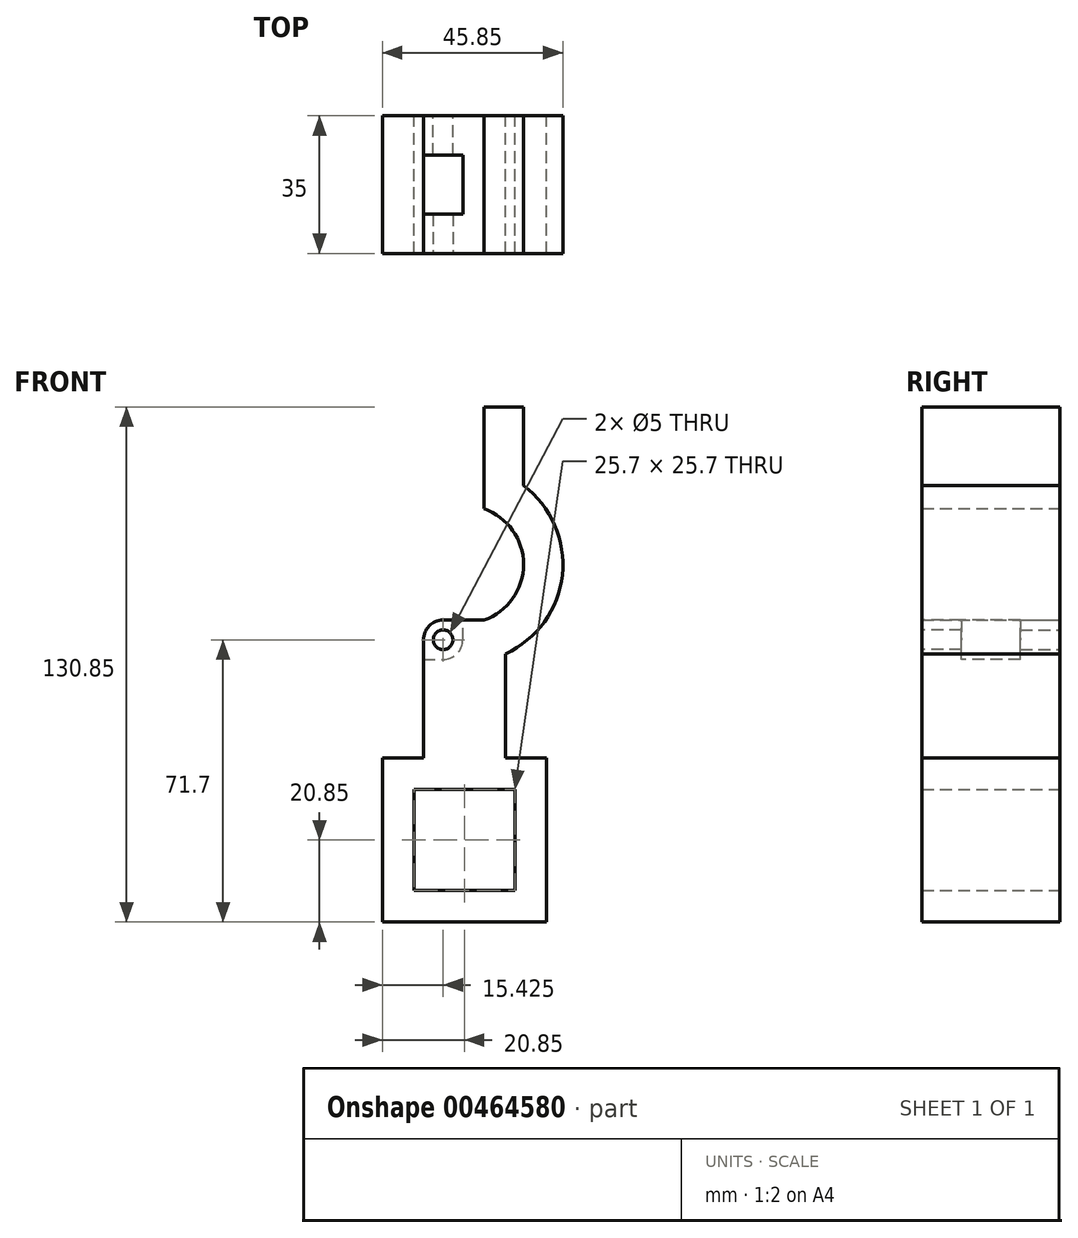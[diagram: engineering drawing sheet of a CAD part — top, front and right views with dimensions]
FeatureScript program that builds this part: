
annotation { "Feature Type Name" : "Feature", "Feature Type Description" : "" }
export const myFeature = defineFeature(function(context is Context, id is Id, definition is map)
    precondition{}
    {
        {
            var Q0;
            Q0=qCreatedBy(makeId("Front.planeOp"),FACE);
            var sketch = newSketch(context, id + "F0", { "sketchPlane" : qUnion([Q0])});
            skLineSegment(sketch, "E0", {"start": v(0, 0) * mm, "end": v(0, 12.85) * mm, "construction": true});
            skLineSegment(sketch, "E1", {"start": v(0, 12.85) * mm, "end": v(12.85, 12.85) * mm});
            skLineSegment(sketch, "E2", {"start": v(12.85, 12.85) * mm, "end": v(12.85, 0) * mm});
            skLineSegment(sketch, "E3", {"start": v(12.85, 0) * mm, "end": v(0, 0) * mm, "construction": true});
            skLineSegment(sketch, "E4", {"start": v(12.85, 0) * mm, "end": v(12.85, -12.85) * mm});
            skLineSegment(sketch, "E5", {"start": v(12.85, -12.85) * mm, "end": v(0, -12.85) * mm});
            skLineSegment(sketch, "E6", {"start": v(0, -12.85) * mm, "end": v(0, 0) * mm, "construction": true});
            skLineSegment(sketch, "E7", {"start": v(0, 0) * mm, "end": v(-12.85, 0) * mm, "construction": true});
            skLineSegment(sketch, "E8", {"start": v(-12.85, 0) * mm, "end": v(-12.85, 12.85) * mm});
            skLineSegment(sketch, "E9", {"start": v(-12.85, 12.85) * mm, "end": v(0, 12.85) * mm});
            skLineSegment(sketch, "E10", {"start": v(-12.85, 0) * mm, "end": v(-12.85, -12.85) * mm});
            skLineSegment(sketch, "E11", {"start": v(-12.85, -12.85) * mm, "end": v(0, -12.85) * mm});
            skLineSegment(sketch, "E12", {"start": v(-12.85, 0) * mm, "end": v(-20.85, 0) * mm, "construction": true});
            skLineSegment(sketch, "E13", {"start": v(-20.85, 0) * mm, "end": v(-20.85, -20.85) * mm});
            skLineSegment(sketch, "E14", {"start": v(20.85, -20.85) * mm, "end": v(20.85, 0) * mm});
            skLineSegment(sketch, "E15", {"start": v(20.85, 0) * mm, "end": v(12.85, 0) * mm, "construction": true});
            skLineSegment(sketch, "E16", {"start": v(20.85, 0) * mm, "end": v(20.85, 20.85) * mm});
            skLineSegment(sketch, "E17", {"start": v(20.85, 20.85) * mm, "end": v(10.43, 20.85) * mm});
            skLineSegment(sketch, "E18", {"start": v(-20.85, 20.85) * mm, "end": v(-20.85, 0) * mm});
            skLineSegment(sketch, "E19", {"start": v(0, 20.85) * mm, "end": v(0, 12.85) * mm, "construction": true});
            skLineSegment(sketch, "E20", {"start": v(-20.85, -20.85) * mm, "end": v(0, -20.85) * mm});
            skLineSegment(sketch, "E21", {"start": v(0, -20.85) * mm, "end": v(20.85, -20.85) * mm});
            skLineSegment(sketch, "E22", {"start": v(0, -12.85) * mm, "end": v(0, -20.85) * mm, "construction": true});
            skLineSegment(sketch, "E23", {"start": v(10.43, 20.85) * mm, "end": v(10.43, 47.28) * mm});
            skLineSegment(sketch, "E24", {"start": v(-10.43, 20.85) * mm, "end": v(-10.43, 55.85) * mm});
            skLineSegment(sketch, "E25", {"start": v(-10.43, 55.85) * mm, "end": v(4.98, 55.85) * mm});
            skArc(sketch, "E26", {"start": v(10.43, 47.28) * mm, "mid": v(24.86, 67.34) * mm, "end": v(15, 90) * mm});
            skArc(sketch, "E27", {"start": v(4.98, 55.85) * mm, "mid": v(15, 69.99) * mm, "end": v(5, 84.14) * mm});
            skLineSegment(sketch, "E28", {"start": v(0, 70) * mm, "end": v(0, 110) * mm, "construction": true});
            skLineSegment(sketch, "E29", {"start": v(0, 110) * mm, "end": v(5, 110) * mm, "construction": true});
            skLineSegment(sketch, "E30", {"start": v(5, 110) * mm, "end": v(5, 84.14) * mm});
            skLineSegment(sketch, "E31", {"start": v(15, 90) * mm, "end": v(15, 110) * mm});
            skLineSegment(sketch, "E32", {"start": v(15, 110) * mm, "end": v(5, 110) * mm});
            skLineSegment(sketch, "E33", {"start": v(0, 110) * mm, "end": v(-5, 110) * mm, "construction": true});
            skLineSegment(sketch, "E34", {"start": v(-5.43, 55.85) * mm, "end": v(-5.43, 50.85) * mm, "construction": true});
            skLineSegment(sketch, "E35", {"start": v(-5.42, 50.85) * mm, "end": v(-10.43, 50.85) * mm, "construction": true});
            skCircle(sketch, "E36", {"center": v(-5.43, 50.85) * mm, "radius": 2.5 * mm});
            skPoint(sketch, "E37.orphan", {"position": v(10.43, 55.85) * mm});
            skLineSegment(sketch, "E38", {"start": v(-20.85, 20.85) * mm, "end": v(-10.43, 20.85) * mm});
            skSolve(sketch);
        }
        {
            var Q0;
            Q0=qSketchRegion(id+"F0",true);
            extrude(context, id + "F1", {"entities" : qUnion([Q0]), "depth" : 15 * mm});
        }
        {
            var Q0;
            Q0=makeQuery(id+"F1.opExtrude","SWEPT_EDGE",EDGE,{"disambiguationData":[OSD([sQuery(id+"F0.wireOp",EDGE,"E24"),sQuery(id+"F0.wireOp",EDGE,"E25")])]});
            fillet(context, id + "F2", {"entities" : qUnion([Q0]), "radius" : 5 * mm, "tangentPropagation" : true, "allowEdgeOverflow" : false});
        }
        {
            var Q0;
            Q0=makeQuery(id+"F1.opExtrude","CAP_FACE",FACE,{"disambiguationData":[OSD([sQuery(id+"F0.wireOp",EDGE,"E1"),sQuery(id+"F0.wireOp",EDGE,"E2"),sQuery(id+"F0.wireOp",EDGE,"E4"),sQuery(id+"F0.wireOp",EDGE,"E5"),sQuery(id+"F0.wireOp",EDGE,"E8"),sQuery(id+"F0.wireOp",EDGE,"E9"),sQuery(id+"F0.wireOp",EDGE,"E10"),sQuery(id+"F0.wireOp",EDGE,"E11"),sQuery(id+"F0.wireOp",EDGE,"E13"),sQuery(id+"F0.wireOp",EDGE,"E14"),sQuery(id+"F0.wireOp",EDGE,"E16"),sQuery(id+"F0.wireOp",EDGE,"E17"),sQuery(id+"F0.wireOp",EDGE,"E18"),sQuery(id+"F0.wireOp",EDGE,"E20"),sQuery(id+"F0.wireOp",EDGE,"E21"),sQuery(id+"F0.wireOp",EDGE,"E23"),sQuery(id+"F0.wireOp",EDGE,"E24"),sQuery(id+"F0.wireOp",EDGE,"E25"),sQuery(id+"F0.wireOp",EDGE,"E26"),sQuery(id+"F0.wireOp",EDGE,"E27"),sQuery(id+"F0.wireOp",EDGE,"E30"),sQuery(id+"F0.wireOp",EDGE,"E31"),sQuery(id+"F0.wireOp",EDGE,"E32"),sQuery(id+"F0.wireOp",EDGE,"E36"),sQuery(id+"F0.wireOp",EDGE,"E38")])],"isStart":false});
            var sketch = newSketch(context, id + "F3", { "sketchPlane" : qUnion([Q0])});
            skArc(sketch, "E39", {"start": v(-5.43, 55.85) * mm, "mid": v(-8.96, 54.39) * mm, "end": v(-10.43, 50.85) * mm});
            skLineSegment(sketch, "E40", {"start": v(-5.43, 50.85) * mm, "end": v(-0.43, 50.85) * mm, "construction": true});
            skLineSegment(sketch, "E41", {"start": v(-0.43, 50.85) * mm, "end": v(-0.43, 55.85) * mm});
            skLineSegment(sketch, "E42", {"start": v(-5.43, 50.85) * mm, "end": v(-5.43, 45.85) * mm, "construction": true});
            skLineSegment(sketch, "E43", {"start": v(-5.43, 50.85) * mm, "end": v(-10.43, 50.85) * mm, "construction": true});
            skLineSegment(sketch, "E44", {"start": v(-10.43, 50.85) * mm, "end": v(-10.43, 45.85) * mm});
            skLineSegment(sketch, "E45", {"start": v(-10.43, 45.85) * mm, "end": v(-5.43, 45.85) * mm});
            skLineSegment(sketch, "E46", {"start": v(-5.43, 50.85) * mm, "end": v(-5.43, 55.85) * mm, "construction": true});
            skLineSegment(sketch, "E47", {"start": v(-5.43, 55.85) * mm, "end": v(-0.43, 55.85) * mm});
            skArc(sketch, "E48.trimOffspring", {"start": v(-5.43, 45.85) * mm, "mid": v(-1.89, 47.31) * mm, "end": v(-0.43, 50.85) * mm});
            skSolve(sketch);
        }
        {
            var Q0;
            Q0=qSketchRegion(id+"F3",true);
            extrude(context, id + "F4", {"entities" : qUnion([Q0]), "operationType" : NewBodyOperationType.REMOVE, "oppositeDirection" : true, "depth" : 5 * mm});
        }
        {
            var Q0;
            Q0=makeQuery(id+"F1.opExtrude","CAP_FACE",FACE,{"disambiguationData":[OSD([sQuery(id+"F0.wireOp",EDGE,"E1"),sQuery(id+"F0.wireOp",EDGE,"E2"),sQuery(id+"F0.wireOp",EDGE,"E4"),sQuery(id+"F0.wireOp",EDGE,"E5"),sQuery(id+"F0.wireOp",EDGE,"E8"),sQuery(id+"F0.wireOp",EDGE,"E9"),sQuery(id+"F0.wireOp",EDGE,"E10"),sQuery(id+"F0.wireOp",EDGE,"E11"),sQuery(id+"F0.wireOp",EDGE,"E13"),sQuery(id+"F0.wireOp",EDGE,"E14"),sQuery(id+"F0.wireOp",EDGE,"E16"),sQuery(id+"F0.wireOp",EDGE,"E17"),sQuery(id+"F0.wireOp",EDGE,"E18"),sQuery(id+"F0.wireOp",EDGE,"E20"),sQuery(id+"F0.wireOp",EDGE,"E21"),sQuery(id+"F0.wireOp",EDGE,"E23"),sQuery(id+"F0.wireOp",EDGE,"E24"),sQuery(id+"F0.wireOp",EDGE,"E25"),sQuery(id+"F0.wireOp",EDGE,"E26"),sQuery(id+"F0.wireOp",EDGE,"E27"),sQuery(id+"F0.wireOp",EDGE,"E30"),sQuery(id+"F0.wireOp",EDGE,"E31"),sQuery(id+"F0.wireOp",EDGE,"E32"),sQuery(id+"F0.wireOp",EDGE,"E36"),sQuery(id+"F0.wireOp",EDGE,"E38")])],"isStart":false});
            extrude(context, id + "F5", {"entities" : qUnion([Q0]), "operationType" : NewBodyOperationType.ADD, "depth" : 2.5 * mm});
        }
        {
            var Q0;
            Q0=qCreatedBy(makeId("Front.planeOp"),FACE);
            cPlane(context, id + "F6", {"entities" : qUnion([Q0]), "cplaneType" : CPlaneType.OFFSET, "offset" : 17.5 * mm, "width" : 150 * mm, "height" : 150 * mm});
        }
        {
            var Q0;
            Q0=makeQuery(id+"F1.opExtrude","SWEPT_BODY",BODY,{"disambiguationData":[OSD([sQuery(id+"F0.wireOp",EDGE,"E1"),sQuery(id+"F0.wireOp",EDGE,"E2"),sQuery(id+"F0.wireOp",EDGE,"E4"),sQuery(id+"F0.wireOp",EDGE,"E5"),sQuery(id+"F0.wireOp",EDGE,"E8"),sQuery(id+"F0.wireOp",EDGE,"E9"),sQuery(id+"F0.wireOp",EDGE,"E10"),sQuery(id+"F0.wireOp",EDGE,"E11"),sQuery(id+"F0.wireOp",EDGE,"E13"),sQuery(id+"F0.wireOp",EDGE,"E14"),sQuery(id+"F0.wireOp",EDGE,"E16"),sQuery(id+"F0.wireOp",EDGE,"E17"),sQuery(id+"F0.wireOp",EDGE,"E18"),sQuery(id+"F0.wireOp",EDGE,"E20"),sQuery(id+"F0.wireOp",EDGE,"E21"),sQuery(id+"F0.wireOp",EDGE,"E23"),sQuery(id+"F0.wireOp",EDGE,"E24"),sQuery(id+"F0.wireOp",EDGE,"E25"),sQuery(id+"F0.wireOp",EDGE,"E26"),sQuery(id+"F0.wireOp",EDGE,"E27"),sQuery(id+"F0.wireOp",EDGE,"E30"),sQuery(id+"F0.wireOp",EDGE,"E31"),sQuery(id+"F0.wireOp",EDGE,"E32"),sQuery(id+"F0.wireOp",EDGE,"E36"),sQuery(id+"F0.wireOp",EDGE,"E38")])]});
            var Q1;
            Q1=qCreatedBy(id+"F6.planeOp",FACE);
            mirror(context, id + "F7", {"operationType" : NewBodyOperationType.ADD, "entities" : qUnion([Q0]), "mirrorPlane" : qUnion([Q1])});
        }
    });
